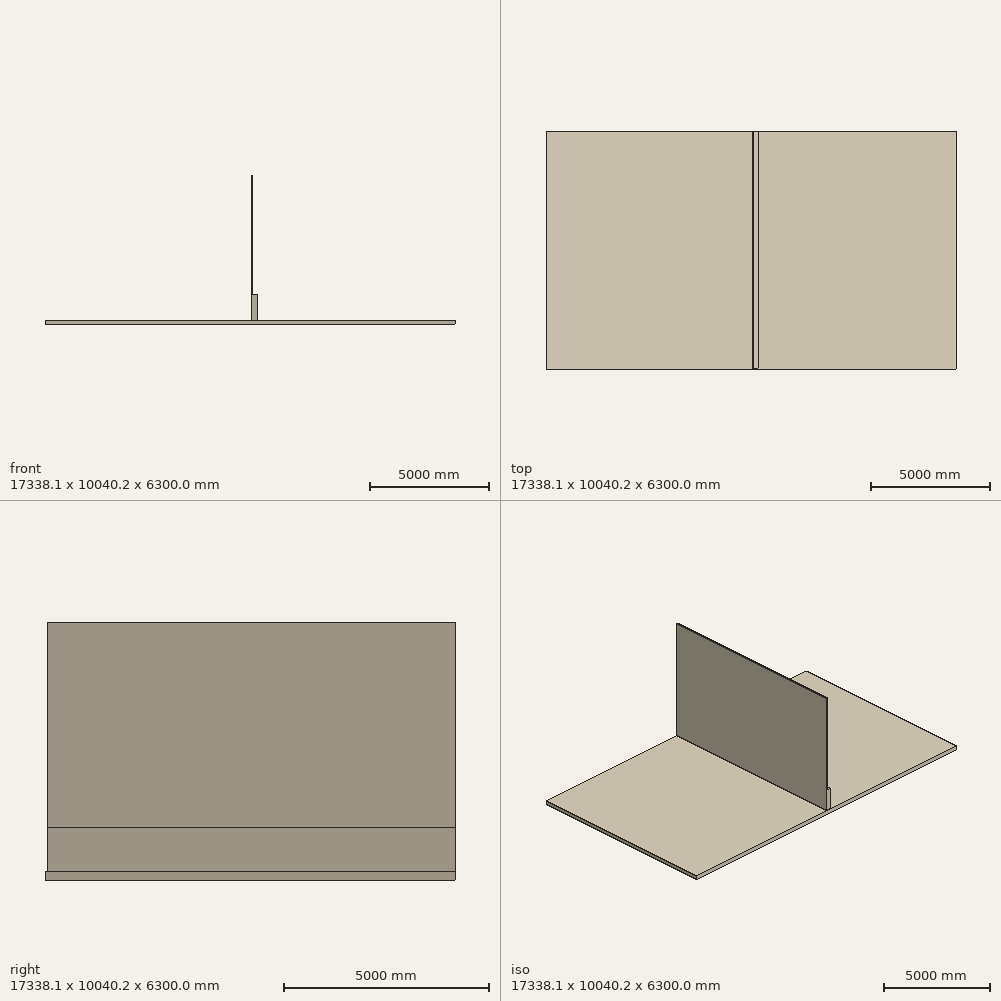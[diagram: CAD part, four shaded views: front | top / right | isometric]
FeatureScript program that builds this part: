
annotation { "Feature Type Name" : "Feature", "Feature Type Description" : "" }
export const myFeature = defineFeature(function(context is Context, id is Id, definition is map)
    precondition{}
    {
        {
            var Q0;
            Q0=qCreatedBy(makeId("Front.planeOp"),FACE);
            var sketch = newSketch(context, id + "F0", { "sketchPlane" : qUnion([Q0])});
            skLineSegment(sketch, "E0.bottom", {"start": v(0, 0) * mm, "end": v(270, 0) * mm});
            skLineSegment(sketch, "E0.top", {"start": v(0, 1100) * mm, "end": v(270, 1100) * mm});
            skLineSegment(sketch, "E0.left", {"start": v(0, 0) * mm, "end": v(0, 1100) * mm});
            skLineSegment(sketch, "E0.right", {"start": v(270, 0) * mm, "end": v(270, 1100) * mm});
            skLineSegment(sketch, "E1.bottom", {"start": v(0, 1100) * mm, "end": v(70, 1100) * mm});
            skLineSegment(sketch, "E1.top", {"start": v(0, 6100) * mm, "end": v(70, 6100) * mm});
            skLineSegment(sketch, "E1.left", {"start": v(0, 1100) * mm, "end": v(0, 6100) * mm});
            skLineSegment(sketch, "E1.right", {"start": v(70, 1100) * mm, "end": v(70, 6100) * mm});
            skSolve(sketch);
        }
        {
            var Q0;
            Q0 = qSketchRegion(id + "F0", true);
            extrude(context, id + "F1", {"entities" : qUnion([Q0]), "depth" : 10000 * mm});
        }
        {
            var Q0;
            Q0=qCreatedBy(makeId("Top.planeOp"),FACE);
            var sketch = newSketch(context, id + "F2", { "sketchPlane" : qUnion([Q0])});
            skLineSegment(sketch, "E2.bottom", {"start": v(-8702.38, 0) * mm, "end": v(8635.69, 0) * mm});
            skLineSegment(sketch, "E2.top", {"start": v(-8702.38, -10040.2) * mm, "end": v(8635.69, -10040.2) * mm});
            skLineSegment(sketch, "E2.left", {"start": v(-8702.38, 0) * mm, "end": v(-8702.38, -10040.2) * mm});
            skLineSegment(sketch, "E2.right", {"start": v(8635.69, 0) * mm, "end": v(8635.69, -10040.2) * mm});
            skSolve(sketch);
        }
        {
            var Q0;
            Q0 = qSketchRegion(id + "F2", true);
            extrude(context, id + "F3", {"entities" : qUnion([Q0]), "operationType" : NewBodyOperationType.ADD, "oppositeDirection" : true, "depth" : 200 * mm});
        }
    });
